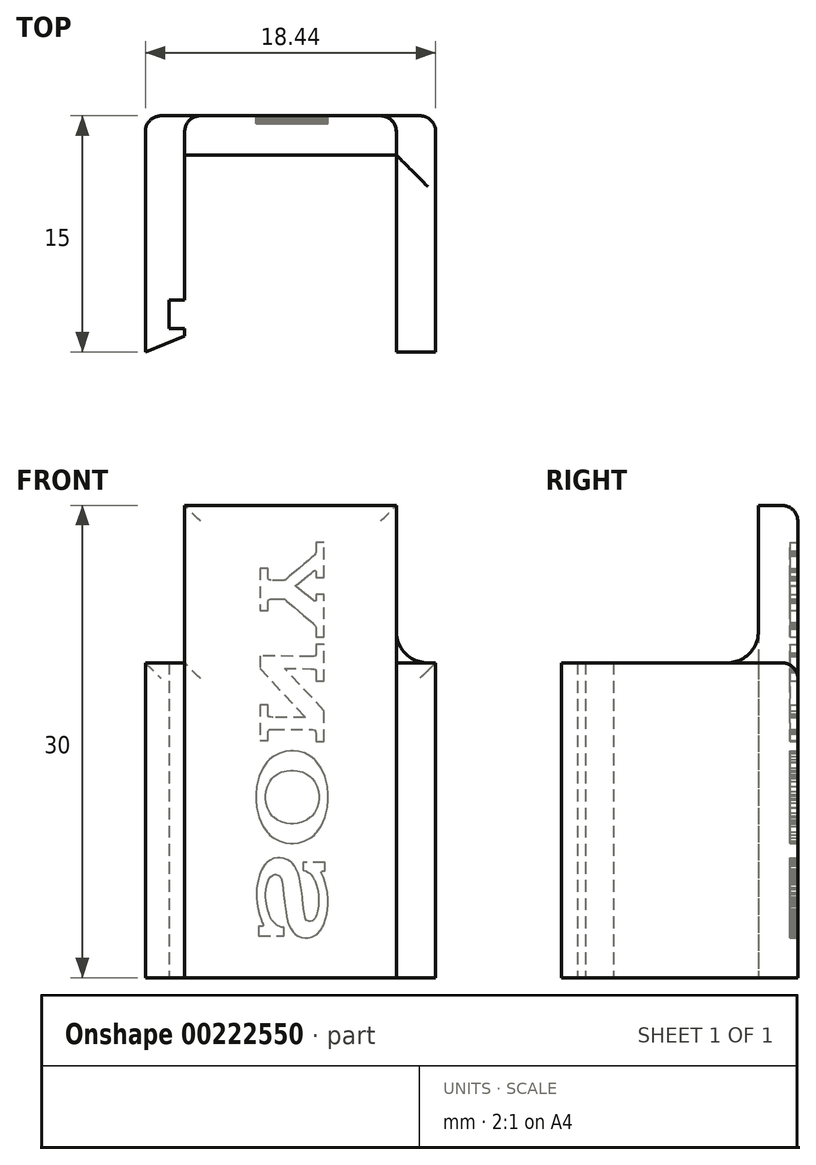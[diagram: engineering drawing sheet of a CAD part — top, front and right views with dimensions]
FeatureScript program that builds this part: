
annotation { "Feature Type Name" : "Feature", "Feature Type Description" : "" }
export const myFeature = defineFeature(function(context is Context, id is Id, definition is map)
    precondition{}
    {
        {
            var Q0;
            Q0=qCreatedBy(makeId("Top.planeOp"),FACE);
            var sketch = newSketch(context, id + "F0", { "sketchPlane" : qUnion([Q0])});
            skLineSegment(sketch, "E0", {"start": v(0, 0) * mm, "end": v(0, 1.5) * mm});
            skLineSegment(sketch, "E1", {"start": v(0, 12.5) * mm, "end": v(13.44, 12.5) * mm});
            skLineSegment(sketch, "E2", {"start": v(13.44, 0) * mm, "end": v(15.94, 0) * mm});
            skLineSegment(sketch, "E3", {"start": v(15.94, 0) * mm, "end": v(15.94, 15) * mm});
            skLineSegment(sketch, "E4", {"start": v(15.94, 15) * mm, "end": v(-2.5, 15) * mm});
            skLineSegment(sketch, "E5", {"start": v(-2.5, 15) * mm, "end": v(-2.5, 0) * mm});
            skLineSegment(sketch, "E6", {"start": v(-2.5, 0) * mm, "end": v(0, 0) * mm});
            skLineSegment(sketch, "E7", {"start": v(13.44, 12.5) * mm, "end": v(13.44, 0) * mm});
            skLineSegment(sketch, "E8", {"start": v(0, 1.5) * mm, "end": v(-1, 1.5) * mm});
            skLineSegment(sketch, "E9", {"start": v(-1, 1.5) * mm, "end": v(-1, 3.3) * mm});
            skLineSegment(sketch, "E10", {"start": v(-1, 3.3) * mm, "end": v(0, 3.3) * mm});
            skLineSegment(sketch, "E11.trimOffspring", {"start": v(0, 3.3) * mm, "end": v(0, 12.5) * mm});
            skSolve(sketch);
        }
        {
            var Q0;
            Q0 = qSketchRegion(id + "F0", true);
            extrude(context, id + "F1", {"entities" : qUnion([Q0]), "depth" : 20 * mm});
        }
        {
            var Q0;
            Q0=makeQuery(id+"F1.opExtrude","CAP_FACE",FACE,{"disambiguationData":[OSD([sQuery(id+"F0.wireOp",EDGE,"E0"),sQuery(id+"F0.wireOp",EDGE,"E1"),sQuery(id+"F0.wireOp",EDGE,"E2"),sQuery(id+"F0.wireOp",EDGE,"E3"),sQuery(id+"F0.wireOp",EDGE,"E4"),sQuery(id+"F0.wireOp",EDGE,"E5"),sQuery(id+"F0.wireOp",EDGE,"E6"),sQuery(id+"F0.wireOp",EDGE,"E7"),sQuery(id+"F0.wireOp",EDGE,"E8"),sQuery(id+"F0.wireOp",EDGE,"E9"),sQuery(id+"F0.wireOp",EDGE,"E10"),sQuery(id+"F0.wireOp",EDGE,"E11.trimOffspring")])],"isStart":false});
            var sketch = newSketch(context, id + "F2", { "sketchPlane" : qUnion([Q0])});
            skLineSegment(sketch, "E12.bottom", {"start": v(0, 15) * mm, "end": v(13.44, 15) * mm});
            skLineSegment(sketch, "E12.top", {"start": v(0, 12.5) * mm, "end": v(13.44, 12.5) * mm});
            skLineSegment(sketch, "E12.left", {"start": v(0, 15) * mm, "end": v(0, 12.5) * mm});
            skLineSegment(sketch, "E12.right", {"start": v(13.44, 15) * mm, "end": v(13.44, 12.5) * mm});
            skSolve(sketch);
        }
        {
            var Q0;
            Q0 = qSketchRegion(id + "F2", true);
            extrude(context, id + "F3", {"entities" : qUnion([Q0]), "operationType" : NewBodyOperationType.ADD, "depth" : 10 * mm});
        }
        {
            var Q0;
            Q0=makeQuery(id+"F3.boolean.opBoolean","MERGE",FACE,{"derivedFrom":[makeQuery(id+"F1.opExtrude","SWEPT_FACE",FACE,{"disambiguationData":[OSD([sQuery(id+"F0.wireOp",EDGE,"E4")])]}),makeQuery(id+"F3.opExtrude","SWEPT_FACE",FACE,{"disambiguationData":[OSD([sQuery(id+"F2.wireOp",EDGE,"E12.bottom")])]})]});
            var sketch = newSketch(context, id + "F4", { "sketchPlane" : qUnion([Q0])});
            skLineSegment(sketch, "E13", {"start": v(-8.35, 27.15) * mm, "end": v(-8.35, 27.12) * mm});
            skLineSegment(sketch, "E14", {"start": v(-8.35, 27.12) * mm, "end": v(-8.34, 27.03) * mm});
            skLineSegment(sketch, "E15", {"start": v(-8.34, 27.03) * mm, "end": v(-8.31, 26.94) * mm});
            skLineSegment(sketch, "E16", {"start": v(-8.31, 26.94) * mm, "end": v(-8.25, 26.85) * mm});
            skLineSegment(sketch, "E17", {"start": v(-8.25, 26.85) * mm, "end": v(-8.18, 26.78) * mm});
            skLineSegment(sketch, "E18", {"start": v(-8.18, 26.78) * mm, "end": v(-8.16, 26.76) * mm});
            skLineSegment(sketch, "E19", {"start": v(-8.16, 26.76) * mm, "end": v(-8.14, 26.75) * mm});
            skLineSegment(sketch, "E20", {"start": v(-8.14, 26.75) * mm, "end": v(-8.06, 26.68) * mm});
            skLineSegment(sketch, "E21", {"start": v(-8.06, 26.68) * mm, "end": v(-7.85, 26.5) * mm});
            skLineSegment(sketch, "E22", {"start": v(-7.85, 26.5) * mm, "end": v(-7.57, 26.27) * mm});
            skLineSegment(sketch, "E23", {"start": v(-7.57, 26.27) * mm, "end": v(-7.26, 26) * mm});
            skLineSegment(sketch, "E24", {"start": v(-7.26, 26) * mm, "end": v(-6.94, 25.74) * mm});
            skLineSegment(sketch, "E25", {"start": v(-6.94, 25.74) * mm, "end": v(-6.67, 25.5) * mm});
            skLineSegment(sketch, "E26", {"start": v(-6.67, 25.5) * mm, "end": v(-6.47, 25.34) * mm});
            skLineSegment(sketch, "E27", {"start": v(-6.47, 25.34) * mm, "end": v(-6.4, 25.28) * mm});
            skLineSegment(sketch, "E28", {"start": v(-6.4, 25.28) * mm, "end": v(-6.38, 25.27) * mm});
            skLineSegment(sketch, "E29", {"start": v(-6.38, 25.27) * mm, "end": v(-6.38, 25.26) * mm});
            skLineSegment(sketch, "E30", {"start": v(-6.38, 25.26) * mm, "end": v(-6.34, 25.25) * mm});
            skLineSegment(sketch, "E31", {"start": v(-6.34, 25.25) * mm, "end": v(-6.32, 25.25) * mm});
            skLineSegment(sketch, "E32", {"start": v(-6.32, 25.25) * mm, "end": v(-6.3, 25.25) * mm});
            skLineSegment(sketch, "E33", {"start": v(-6.3, 25.25) * mm, "end": v(-5.5, 25.25) * mm});
            skLineSegment(sketch, "E34", {"start": v(-5.5, 25.25) * mm, "end": v(-5.49, 25.25) * mm});
            skLineSegment(sketch, "E35", {"start": v(-5.49, 25.25) * mm, "end": v(-5.44, 25.25) * mm});
            skLineSegment(sketch, "E36", {"start": v(-5.44, 25.25) * mm, "end": v(-5.4, 25.26) * mm});
            skLineSegment(sketch, "E37", {"start": v(-5.4, 25.26) * mm, "end": v(-5.39, 25.26) * mm});
            skLineSegment(sketch, "E38", {"start": v(-5.39, 25.26) * mm, "end": v(-5.38, 25.26) * mm});
            skLineSegment(sketch, "E39", {"start": v(-5.38, 25.26) * mm, "end": v(-5.33, 25.3) * mm});
            skLineSegment(sketch, "E40", {"start": v(-5.33, 25.3) * mm, "end": v(-5.3, 25.35) * mm});
            skLineSegment(sketch, "E41", {"start": v(-5.3, 25.35) * mm, "end": v(-5.3, 25.37) * mm});
            skLineSegment(sketch, "E42", {"start": v(-5.3, 25.37) * mm, "end": v(-5.29, 25.37) * mm});
            skLineSegment(sketch, "E43", {"start": v(-5.29, 25.37) * mm, "end": v(-5.28, 25.43) * mm});
            skLineSegment(sketch, "E44", {"start": v(-5.28, 25.43) * mm, "end": v(-5.28, 25.48) * mm});
            skLineSegment(sketch, "E45", {"start": v(-5.28, 25.48) * mm, "end": v(-5.28, 25.5) * mm});
            skLineSegment(sketch, "E46", {"start": v(-5.28, 25.5) * mm, "end": v(-5.28, 26) * mm});
            skLineSegment(sketch, "E47", {"start": v(-5.28, 26) * mm, "end": v(-4.77, 26) * mm});
            skLineSegment(sketch, "E48", {"start": v(-4.77, 26) * mm, "end": v(-4.77, 23.31) * mm});
            skLineSegment(sketch, "E49", {"start": v(-4.77, 23.31) * mm, "end": v(-5.28, 23.31) * mm});
            skLineSegment(sketch, "E50", {"start": v(-5.28, 23.31) * mm, "end": v(-5.28, 23.8) * mm});
            skLineSegment(sketch, "E51", {"start": v(-5.28, 23.8) * mm, "end": v(-5.28, 23.81) * mm});
            skLineSegment(sketch, "E52", {"start": v(-5.28, 23.81) * mm, "end": v(-5.28, 23.86) * mm});
            skLineSegment(sketch, "E53", {"start": v(-5.28, 23.86) * mm, "end": v(-5.29, 23.93) * mm});
            skLineSegment(sketch, "E54", {"start": v(-5.29, 23.93) * mm, "end": v(-5.3, 23.93) * mm});
            skLineSegment(sketch, "E55", {"start": v(-5.3, 23.93) * mm, "end": v(-5.3, 23.94) * mm});
            skLineSegment(sketch, "E56", {"start": v(-5.3, 23.94) * mm, "end": v(-5.33, 24) * mm});
            skLineSegment(sketch, "E57", {"start": v(-5.33, 24) * mm, "end": v(-5.38, 24.03) * mm});
            skLineSegment(sketch, "E58", {"start": v(-5.38, 24.03) * mm, "end": v(-5.39, 24.04) * mm});
            skLineSegment(sketch, "E59", {"start": v(-5.39, 24.04) * mm, "end": v(-5.4, 24.04) * mm});
            skLineSegment(sketch, "E60", {"start": v(-5.4, 24.04) * mm, "end": v(-5.44, 24.05) * mm});
            skLineSegment(sketch, "E61", {"start": v(-5.44, 24.05) * mm, "end": v(-5.49, 24.05) * mm});
            skLineSegment(sketch, "E62", {"start": v(-5.49, 24.05) * mm, "end": v(-5.5, 24.05) * mm});
            skLineSegment(sketch, "E63", {"start": v(-5.5, 24.05) * mm, "end": v(-5.62, 24.05) * mm});
            skLineSegment(sketch, "E64", {"start": v(-5.62, 24.05) * mm, "end": v(-5.9, 24.05) * mm});
            skLineSegment(sketch, "E65", {"start": v(-5.9, 24.05) * mm, "end": v(-6.17, 24.05) * mm});
            skLineSegment(sketch, "E66", {"start": v(-6.17, 24.05) * mm, "end": v(-6.27, 24.05) * mm});
            skLineSegment(sketch, "E67", {"start": v(-6.27, 24.05) * mm, "end": v(-6.3, 24.05) * mm});
            skLineSegment(sketch, "E68", {"start": v(-6.3, 24.05) * mm, "end": v(-6.31, 24.05) * mm});
            skLineSegment(sketch, "E69", {"start": v(-6.31, 24.05) * mm, "end": v(-6.33, 24.04) * mm});
            skLineSegment(sketch, "E70", {"start": v(-6.33, 24.04) * mm, "end": v(-6.37, 24.02) * mm});
            skLineSegment(sketch, "E71", {"start": v(-6.37, 24.02) * mm, "end": v(-6.38, 24.02) * mm});
            skLineSegment(sketch, "E72", {"start": v(-6.38, 24.02) * mm, "end": v(-6.39, 24) * mm});
            skLineSegment(sketch, "E73", {"start": v(-6.39, 24) * mm, "end": v(-6.46, 23.94) * mm});
            skLineSegment(sketch, "E74", {"start": v(-6.46, 23.94) * mm, "end": v(-6.66, 23.78) * mm});
            skLineSegment(sketch, "E75", {"start": v(-6.66, 23.78) * mm, "end": v(-6.93, 23.55) * mm});
            skLineSegment(sketch, "E76", {"start": v(-6.93, 23.55) * mm, "end": v(-7.24, 23.29) * mm});
            skLineSegment(sketch, "E77", {"start": v(-7.24, 23.29) * mm, "end": v(-7.55, 23.02) * mm});
            skLineSegment(sketch, "E78", {"start": v(-7.55, 23.02) * mm, "end": v(-7.83, 22.79) * mm});
            skLineSegment(sketch, "E79", {"start": v(-7.83, 22.79) * mm, "end": v(-8.03, 22.62) * mm});
            skLineSegment(sketch, "E80", {"start": v(-8.03, 22.62) * mm, "end": v(-8.1, 22.55) * mm});
            skLineSegment(sketch, "E81", {"start": v(-8.1, 22.55) * mm, "end": v(-8.12, 22.54) * mm});
            skLineSegment(sketch, "E82", {"start": v(-8.12, 22.54) * mm, "end": v(-8.14, 22.52) * mm});
            skLineSegment(sketch, "E83", {"start": v(-8.14, 22.52) * mm, "end": v(-8.2, 22.47) * mm});
            skLineSegment(sketch, "E84", {"start": v(-8.2, 22.47) * mm, "end": v(-8.27, 22.37) * mm});
            skLineSegment(sketch, "E85", {"start": v(-8.27, 22.37) * mm, "end": v(-8.33, 22.26) * mm});
            skLineSegment(sketch, "E86", {"start": v(-8.33, 22.26) * mm, "end": v(-8.35, 22.15) * mm});
            skLineSegment(sketch, "E87", {"start": v(-8.35, 22.15) * mm, "end": v(-8.35, 22.11) * mm});
            skLineSegment(sketch, "E88", {"start": v(-8.35, 22.11) * mm, "end": v(-8.35, 21.63) * mm});
            skLineSegment(sketch, "E89", {"start": v(-8.35, 21.63) * mm, "end": v(-8.86, 21.63) * mm});
            skLineSegment(sketch, "E90", {"start": v(-8.86, 21.63) * mm, "end": v(-8.86, 24.34) * mm});
            skLineSegment(sketch, "E91", {"start": v(-8.86, 24.34) * mm, "end": v(-8.35, 24.34) * mm});
            skLineSegment(sketch, "E92", {"start": v(-8.35, 24.34) * mm, "end": v(-8.35, 24.01) * mm});
            skLineSegment(sketch, "E93", {"start": v(-8.35, 24.01) * mm, "end": v(-8.35, 24) * mm});
            skLineSegment(sketch, "E94", {"start": v(-8.35, 24) * mm, "end": v(-8.34, 23.96) * mm});
            skLineSegment(sketch, "E95", {"start": v(-8.34, 23.96) * mm, "end": v(-8.3, 23.93) * mm});
            skLineSegment(sketch, "E96", {"start": v(-8.3, 23.93) * mm, "end": v(-8.25, 23.92) * mm});
            skLineSegment(sketch, "E97", {"start": v(-8.25, 23.92) * mm, "end": v(-8.2, 23.94) * mm});
            skLineSegment(sketch, "E98", {"start": v(-8.2, 23.94) * mm, "end": v(-8.2, 23.95) * mm});
            skLineSegment(sketch, "E99", {"start": v(-8.2, 23.95) * mm, "end": v(-8.14, 24) * mm});
            skLineSegment(sketch, "E100", {"start": v(-8.14, 24) * mm, "end": v(-8.01, 24.1) * mm});
            skLineSegment(sketch, "E101", {"start": v(-8.01, 24.1) * mm, "end": v(-7.83, 24.24) * mm});
            skLineSegment(sketch, "E102", {"start": v(-7.83, 24.24) * mm, "end": v(-7.62, 24.4) * mm});
            skLineSegment(sketch, "E103", {"start": v(-7.62, 24.4) * mm, "end": v(-7.41, 24.58) * mm});
            skLineSegment(sketch, "E104", {"start": v(-7.41, 24.58) * mm, "end": v(-7.23, 24.73) * mm});
            skLineSegment(sketch, "E105", {"start": v(-7.23, 24.73) * mm, "end": v(-7.1, 24.83) * mm});
            skLineSegment(sketch, "E106", {"start": v(-7.1, 24.83) * mm, "end": v(-7.05, 24.87) * mm});
            skLineSegment(sketch, "E107", {"start": v(-7.05, 24.87) * mm, "end": v(-7.05, 24.87) * mm});
            skLineSegment(sketch, "E108", {"start": v(-7.05, 24.87) * mm, "end": v(-7.04, 24.87) * mm});
            skLineSegment(sketch, "E109", {"start": v(-7.04, 24.87) * mm, "end": v(-7.04, 24.9) * mm});
            skLineSegment(sketch, "E110", {"start": v(-7.04, 24.9) * mm, "end": v(-7.04, 24.9) * mm});
            skLineSegment(sketch, "E111", {"start": v(-7.04, 24.9) * mm, "end": v(-7.05, 24.9) * mm});
            skLineSegment(sketch, "E112", {"start": v(-7.05, 24.9) * mm, "end": v(-7.1, 24.94) * mm});
            skLineSegment(sketch, "E113", {"start": v(-7.1, 24.94) * mm, "end": v(-7.23, 25.05) * mm});
            skLineSegment(sketch, "E114", {"start": v(-7.23, 25.05) * mm, "end": v(-7.4, 25.2) * mm});
            skLineSegment(sketch, "E115", {"start": v(-7.4, 25.2) * mm, "end": v(-7.62, 25.37) * mm});
            skLineSegment(sketch, "E116", {"start": v(-7.62, 25.37) * mm, "end": v(-7.83, 25.54) * mm});
            skLineSegment(sketch, "E117", {"start": v(-7.83, 25.54) * mm, "end": v(-8, 25.7) * mm});
            skLineSegment(sketch, "E118", {"start": v(-8, 25.7) * mm, "end": v(-8.14, 25.8) * mm});
            skLineSegment(sketch, "E119", {"start": v(-8.14, 25.8) * mm, "end": v(-8.19, 25.84) * mm});
            skLineSegment(sketch, "E120", {"start": v(-8.19, 25.84) * mm, "end": v(-8.2, 25.84) * mm});
            skLineSegment(sketch, "E121", {"start": v(-8.2, 25.84) * mm, "end": v(-8.2, 25.85) * mm});
            skLineSegment(sketch, "E122", {"start": v(-8.2, 25.85) * mm, "end": v(-8.24, 25.86) * mm});
            skLineSegment(sketch, "E123", {"start": v(-8.24, 25.86) * mm, "end": v(-8.3, 25.85) * mm});
            skLineSegment(sketch, "E124", {"start": v(-8.3, 25.85) * mm, "end": v(-8.33, 25.82) * mm});
            skLineSegment(sketch, "E125", {"start": v(-8.33, 25.82) * mm, "end": v(-8.35, 25.78) * mm});
            skLineSegment(sketch, "E126", {"start": v(-8.35, 25.78) * mm, "end": v(-8.35, 25.76) * mm});
            skLineSegment(sketch, "E127", {"start": v(-8.35, 25.76) * mm, "end": v(-8.35, 25.43) * mm});
            skLineSegment(sketch, "E128", {"start": v(-8.35, 25.43) * mm, "end": v(-8.86, 25.43) * mm});
            skLineSegment(sketch, "E129", {"start": v(-8.86, 25.43) * mm, "end": v(-8.86, 27.65) * mm});
            skLineSegment(sketch, "E130", {"start": v(-8.86, 27.65) * mm, "end": v(-8.35, 27.65) * mm});
            skLineSegment(sketch, "E131", {"start": v(-8.35, 27.65) * mm, "end": v(-8.35, 27.15) * mm});
            skLineSegment(sketch, "E132", {"start": v(-8.03, 20.4) * mm, "end": v(-4.77, 20.45) * mm});
            skLineSegment(sketch, "E133", {"start": v(-4.77, 20.45) * mm, "end": v(-4.77, 19.66) * mm});
            skLineSegment(sketch, "E134", {"start": v(-4.77, 19.66) * mm, "end": v(-7.66, 16.54) * mm});
            skLineSegment(sketch, "E135", {"start": v(-7.66, 16.54) * mm, "end": v(-5.6, 16.55) * mm});
            skLineSegment(sketch, "E136", {"start": v(-5.6, 16.55) * mm, "end": v(-5.57, 16.55) * mm});
            skLineSegment(sketch, "E137", {"start": v(-5.57, 16.55) * mm, "end": v(-5.46, 16.55) * mm});
            skLineSegment(sketch, "E138", {"start": v(-5.46, 16.55) * mm, "end": v(-5.36, 16.58) * mm});
            skLineSegment(sketch, "E139", {"start": v(-5.36, 16.58) * mm, "end": v(-5.3, 16.65) * mm});
            skLineSegment(sketch, "E140", {"start": v(-5.3, 16.65) * mm, "end": v(-5.28, 16.75) * mm});
            skLineSegment(sketch, "E141", {"start": v(-5.28, 16.75) * mm, "end": v(-5.28, 16.78) * mm});
            skLineSegment(sketch, "E142", {"start": v(-5.28, 16.78) * mm, "end": v(-5.28, 17.33) * mm});
            skLineSegment(sketch, "E143", {"start": v(-5.28, 17.33) * mm, "end": v(-4.77, 17.33) * mm});
            skLineSegment(sketch, "E144", {"start": v(-4.77, 17.33) * mm, "end": v(-4.77, 15.07) * mm});
            skLineSegment(sketch, "E145", {"start": v(-4.77, 15.07) * mm, "end": v(-5.28, 15.07) * mm});
            skLineSegment(sketch, "E146", {"start": v(-5.28, 15.07) * mm, "end": v(-5.28, 15.6) * mm});
            skLineSegment(sketch, "E147", {"start": v(-5.28, 15.6) * mm, "end": v(-5.28, 15.62) * mm});
            skLineSegment(sketch, "E148", {"start": v(-5.28, 15.62) * mm, "end": v(-5.31, 15.7) * mm});
            skLineSegment(sketch, "E149", {"start": v(-5.31, 15.7) * mm, "end": v(-5.4, 15.76) * mm});
            skLineSegment(sketch, "E150", {"start": v(-5.4, 15.76) * mm, "end": v(-5.5, 15.78) * mm});
            skLineSegment(sketch, "E151", {"start": v(-5.5, 15.78) * mm, "end": v(-5.6, 15.79) * mm});
            skLineSegment(sketch, "E152", {"start": v(-5.6, 15.79) * mm, "end": v(-5.62, 15.79) * mm});
            skLineSegment(sketch, "E153", {"start": v(-5.62, 15.79) * mm, "end": v(-8.01, 15.79) * mm});
            skLineSegment(sketch, "E154", {"start": v(-8.01, 15.79) * mm, "end": v(-8.04, 15.79) * mm});
            skLineSegment(sketch, "E155", {"start": v(-8.04, 15.79) * mm, "end": v(-8.13, 15.78) * mm});
            skLineSegment(sketch, "E156", {"start": v(-8.13, 15.78) * mm, "end": v(-8.24, 15.74) * mm});
            skLineSegment(sketch, "E157", {"start": v(-8.24, 15.74) * mm, "end": v(-8.32, 15.64) * mm});
            skLineSegment(sketch, "E158", {"start": v(-8.32, 15.64) * mm, "end": v(-8.35, 15.5) * mm});
            skLineSegment(sketch, "E159", {"start": v(-8.35, 15.5) * mm, "end": v(-8.35, 15.45) * mm});
            skLineSegment(sketch, "E160", {"start": v(-8.35, 15.45) * mm, "end": v(-8.35, 15.02) * mm});
            skLineSegment(sketch, "E161", {"start": v(-8.35, 15.02) * mm, "end": v(-8.86, 15.02) * mm});
            skLineSegment(sketch, "E162", {"start": v(-8.86, 15.02) * mm, "end": v(-8.86, 16.96) * mm});
            skLineSegment(sketch, "E163", {"start": v(-8.86, 16.96) * mm, "end": v(-6.33, 19.66) * mm});
            skLineSegment(sketch, "E164", {"start": v(-6.33, 19.66) * mm, "end": v(-8.03, 19.63) * mm});
            skLineSegment(sketch, "E165", {"start": v(-8.03, 19.63) * mm, "end": v(-8.07, 19.63) * mm});
            skLineSegment(sketch, "E166", {"start": v(-8.07, 19.63) * mm, "end": v(-8.18, 19.62) * mm});
            skLineSegment(sketch, "E167", {"start": v(-8.18, 19.62) * mm, "end": v(-8.27, 19.58) * mm});
            skLineSegment(sketch, "E168", {"start": v(-8.27, 19.58) * mm, "end": v(-8.33, 19.5) * mm});
            skLineSegment(sketch, "E169", {"start": v(-8.33, 19.5) * mm, "end": v(-8.35, 19.39) * mm});
            skLineSegment(sketch, "E170", {"start": v(-8.35, 19.39) * mm, "end": v(-8.35, 19.35) * mm});
            skLineSegment(sketch, "E171", {"start": v(-8.35, 19.35) * mm, "end": v(-8.35, 18.85) * mm});
            skLineSegment(sketch, "E172", {"start": v(-8.35, 18.85) * mm, "end": v(-8.86, 18.85) * mm});
            skLineSegment(sketch, "E173", {"start": v(-8.86, 18.85) * mm, "end": v(-8.86, 21.16) * mm});
            skLineSegment(sketch, "E174", {"start": v(-8.86, 21.16) * mm, "end": v(-8.35, 21.16) * mm});
            skLineSegment(sketch, "E175", {"start": v(-8.35, 21.16) * mm, "end": v(-8.35, 20.66) * mm});
            skLineSegment(sketch, "E176", {"start": v(-8.35, 20.66) * mm, "end": v(-8.35, 20.62) * mm});
            skLineSegment(sketch, "E177", {"start": v(-8.35, 20.62) * mm, "end": v(-8.33, 20.52) * mm});
            skLineSegment(sketch, "E178", {"start": v(-8.33, 20.52) * mm, "end": v(-8.28, 20.44) * mm});
            skLineSegment(sketch, "E179", {"start": v(-8.28, 20.44) * mm, "end": v(-8.18, 20.41) * mm});
            skLineSegment(sketch, "E180", {"start": v(-8.18, 20.41) * mm, "end": v(-8.07, 20.4) * mm});
            skLineSegment(sketch, "E181", {"start": v(-8.07, 20.4) * mm, "end": v(-8.03, 20.4) * mm});
            skLineSegment(sketch, "E182", {"start": v(-4.52, 11.47) * mm, "end": v(-4.52, 11.3) * mm});
            skLineSegment(sketch, "E183", {"start": v(-4.52, 11.3) * mm, "end": v(-4.57, 10.8) * mm});
            skLineSegment(sketch, "E184", {"start": v(-4.57, 10.8) * mm, "end": v(-4.72, 10.18) * mm});
            skLineSegment(sketch, "E185", {"start": v(-4.72, 10.18) * mm, "end": v(-4.98, 9.63) * mm});
            skLineSegment(sketch, "E186", {"start": v(-4.98, 9.63) * mm, "end": v(-5.23, 9.26) * mm});
            skLineSegment(sketch, "E187", {"start": v(-5.23, 9.26) * mm, "end": v(-5.33, 9.15) * mm});
            skLineSegment(sketch, "E188", {"start": v(-5.33, 9.15) * mm, "end": v(-5.4, 9.08) * mm});
            skLineSegment(sketch, "E189", {"start": v(-5.4, 9.08) * mm, "end": v(-5.65, 8.88) * mm});
            skLineSegment(sketch, "E190", {"start": v(-5.65, 8.88) * mm, "end": v(-6.01, 8.68) * mm});
            skLineSegment(sketch, "E191", {"start": v(-6.01, 8.68) * mm, "end": v(-6.4, 8.56) * mm});
            skLineSegment(sketch, "E192", {"start": v(-6.4, 8.56) * mm, "end": v(-6.72, 8.52) * mm});
            skLineSegment(sketch, "E193", {"start": v(-6.72, 8.52) * mm, "end": v(-6.82, 8.52) * mm});
            skLineSegment(sketch, "E194", {"start": v(-6.82, 8.52) * mm, "end": v(-6.92, 8.52) * mm});
            skLineSegment(sketch, "E195", {"start": v(-6.92, 8.52) * mm, "end": v(-7.23, 8.56) * mm});
            skLineSegment(sketch, "E196", {"start": v(-7.23, 8.56) * mm, "end": v(-7.62, 8.68) * mm});
            skLineSegment(sketch, "E197", {"start": v(-7.62, 8.68) * mm, "end": v(-7.99, 8.88) * mm});
            skLineSegment(sketch, "E198", {"start": v(-7.99, 8.88) * mm, "end": v(-8.24, 9.08) * mm});
            skLineSegment(sketch, "E199", {"start": v(-8.24, 9.08) * mm, "end": v(-8.3, 9.15) * mm});
            skLineSegment(sketch, "E200", {"start": v(-8.3, 9.15) * mm, "end": v(-8.4, 9.26) * mm});
            skLineSegment(sketch, "E201", {"start": v(-8.4, 9.26) * mm, "end": v(-8.65, 9.62) * mm});
            skLineSegment(sketch, "E202", {"start": v(-8.65, 9.62) * mm, "end": v(-8.9, 10.18) * mm});
            skLineSegment(sketch, "E203", {"start": v(-8.9, 10.18) * mm, "end": v(-9.06, 10.82) * mm});
            skLineSegment(sketch, "E204", {"start": v(-9.06, 10.82) * mm, "end": v(-9.12, 11.3) * mm});
            skLineSegment(sketch, "E205", {"start": v(-9.12, 11.3) * mm, "end": v(-9.12, 11.47) * mm});
            skLineSegment(sketch, "E206", {"start": v(-9.12, 11.47) * mm, "end": v(-9.12, 11.64) * mm});
            skLineSegment(sketch, "E207", {"start": v(-9.12, 11.64) * mm, "end": v(-9.07, 12.16) * mm});
            skLineSegment(sketch, "E208", {"start": v(-9.07, 12.16) * mm, "end": v(-8.92, 12.78) * mm});
            skLineSegment(sketch, "E209", {"start": v(-8.92, 12.78) * mm, "end": v(-8.67, 13.32) * mm});
            skLineSegment(sketch, "E210", {"start": v(-8.67, 13.32) * mm, "end": v(-8.41, 13.69) * mm});
            skLineSegment(sketch, "E211", {"start": v(-8.41, 13.69) * mm, "end": v(-8.3, 13.8) * mm});
            skLineSegment(sketch, "E212", {"start": v(-8.3, 13.8) * mm, "end": v(-8.24, 13.87) * mm});
            skLineSegment(sketch, "E213", {"start": v(-8.24, 13.87) * mm, "end": v(-7.99, 14.07) * mm});
            skLineSegment(sketch, "E214", {"start": v(-7.99, 14.07) * mm, "end": v(-7.62, 14.26) * mm});
            skLineSegment(sketch, "E215", {"start": v(-7.62, 14.26) * mm, "end": v(-7.23, 14.38) * mm});
            skLineSegment(sketch, "E216", {"start": v(-7.23, 14.38) * mm, "end": v(-6.92, 14.42) * mm});
            skLineSegment(sketch, "E217", {"start": v(-6.92, 14.42) * mm, "end": v(-6.82, 14.42) * mm});
            skLineSegment(sketch, "E218", {"start": v(-6.82, 14.42) * mm, "end": v(-6.72, 14.42) * mm});
            skLineSegment(sketch, "E219", {"start": v(-6.72, 14.42) * mm, "end": v(-6.42, 14.38) * mm});
            skLineSegment(sketch, "E220", {"start": v(-6.42, 14.38) * mm, "end": v(-6.02, 14.26) * mm});
            skLineSegment(sketch, "E221", {"start": v(-6.02, 14.26) * mm, "end": v(-5.65, 14.07) * mm});
            skLineSegment(sketch, "E222", {"start": v(-5.65, 14.07) * mm, "end": v(-5.4, 13.87) * mm});
            skLineSegment(sketch, "E223", {"start": v(-5.4, 13.87) * mm, "end": v(-5.33, 13.8) * mm});
            skLineSegment(sketch, "E224", {"start": v(-5.33, 13.8) * mm, "end": v(-5.23, 13.7) * mm});
            skLineSegment(sketch, "E225", {"start": v(-5.23, 13.7) * mm, "end": v(-4.98, 13.33) * mm});
            skLineSegment(sketch, "E226", {"start": v(-4.98, 13.33) * mm, "end": v(-4.72, 12.77) * mm});
            skLineSegment(sketch, "E227", {"start": v(-4.72, 12.77) * mm, "end": v(-4.57, 12.14) * mm});
            skLineSegment(sketch, "E228", {"start": v(-4.57, 12.14) * mm, "end": v(-4.52, 11.64) * mm});
            skLineSegment(sketch, "E229", {"start": v(-4.52, 11.64) * mm, "end": v(-4.52, 11.47) * mm});
            skLineSegment(sketch, "E230", {"start": v(-8.02, 12.72) * mm, "end": v(-8.08, 12.66) * mm});
            skLineSegment(sketch, "E231", {"start": v(-8.08, 12.66) * mm, "end": v(-8.23, 12.46) * mm});
            skLineSegment(sketch, "E232", {"start": v(-8.23, 12.46) * mm, "end": v(-8.39, 12.16) * mm});
            skLineSegment(sketch, "E233", {"start": v(-8.39, 12.16) * mm, "end": v(-8.49, 11.82) * mm});
            skLineSegment(sketch, "E234", {"start": v(-8.49, 11.82) * mm, "end": v(-8.52, 11.56) * mm});
            skLineSegment(sketch, "E235", {"start": v(-8.52, 11.56) * mm, "end": v(-8.52, 11.47) * mm});
            skLineSegment(sketch, "E236", {"start": v(-8.52, 11.47) * mm, "end": v(-8.52, 11.38) * mm});
            skLineSegment(sketch, "E237", {"start": v(-8.52, 11.38) * mm, "end": v(-8.49, 11.12) * mm});
            skLineSegment(sketch, "E238", {"start": v(-8.49, 11.12) * mm, "end": v(-8.4, 10.79) * mm});
            skLineSegment(sketch, "E239", {"start": v(-8.4, 10.79) * mm, "end": v(-8.24, 10.48) * mm});
            skLineSegment(sketch, "E240", {"start": v(-8.24, 10.48) * mm, "end": v(-8.08, 10.28) * mm});
            skLineSegment(sketch, "E241", {"start": v(-8.08, 10.28) * mm, "end": v(-8.02, 10.23) * mm});
            skLineSegment(sketch, "E242", {"start": v(-8.02, 10.23) * mm, "end": v(-7.97, 10.17) * mm});
            skLineSegment(sketch, "E243", {"start": v(-7.97, 10.17) * mm, "end": v(-7.77, 10.03) * mm});
            skLineSegment(sketch, "E244", {"start": v(-7.77, 10.03) * mm, "end": v(-7.48, 9.89) * mm});
            skLineSegment(sketch, "E245", {"start": v(-7.48, 9.89) * mm, "end": v(-7.16, 9.8) * mm});
            skLineSegment(sketch, "E246", {"start": v(-7.16, 9.8) * mm, "end": v(-6.9, 9.77) * mm});
            skLineSegment(sketch, "E247", {"start": v(-6.9, 9.77) * mm, "end": v(-6.82, 9.77) * mm});
            skLineSegment(sketch, "E248", {"start": v(-6.82, 9.77) * mm, "end": v(-6.74, 9.77) * mm});
            skLineSegment(sketch, "E249", {"start": v(-6.74, 9.77) * mm, "end": v(-6.48, 9.8) * mm});
            skLineSegment(sketch, "E250", {"start": v(-6.48, 9.8) * mm, "end": v(-6.16, 9.89) * mm});
            skLineSegment(sketch, "E251", {"start": v(-6.16, 9.89) * mm, "end": v(-5.87, 10.03) * mm});
            skLineSegment(sketch, "E252", {"start": v(-5.87, 10.03) * mm, "end": v(-5.68, 10.17) * mm});
            skLineSegment(sketch, "E253", {"start": v(-5.68, 10.17) * mm, "end": v(-5.62, 10.23) * mm});
            skLineSegment(sketch, "E254", {"start": v(-5.62, 10.23) * mm, "end": v(-5.56, 10.28) * mm});
            skLineSegment(sketch, "E255", {"start": v(-5.56, 10.28) * mm, "end": v(-5.4, 10.48) * mm});
            skLineSegment(sketch, "E256", {"start": v(-5.4, 10.48) * mm, "end": v(-5.25, 10.79) * mm});
            skLineSegment(sketch, "E257", {"start": v(-5.25, 10.79) * mm, "end": v(-5.16, 11.12) * mm});
            skLineSegment(sketch, "E258", {"start": v(-5.16, 11.12) * mm, "end": v(-5.12, 11.38) * mm});
            skLineSegment(sketch, "E259", {"start": v(-5.12, 11.38) * mm, "end": v(-5.12, 11.47) * mm});
            skLineSegment(sketch, "E260", {"start": v(-5.12, 11.47) * mm, "end": v(-5.12, 11.56) * mm});
            skLineSegment(sketch, "E261", {"start": v(-5.12, 11.56) * mm, "end": v(-5.16, 11.83) * mm});
            skLineSegment(sketch, "E262", {"start": v(-5.16, 11.83) * mm, "end": v(-5.25, 12.16) * mm});
            skLineSegment(sketch, "E263", {"start": v(-5.25, 12.16) * mm, "end": v(-5.4, 12.46) * mm});
            skLineSegment(sketch, "E264", {"start": v(-5.4, 12.46) * mm, "end": v(-5.56, 12.66) * mm});
            skLineSegment(sketch, "E265", {"start": v(-5.56, 12.66) * mm, "end": v(-5.62, 12.72) * mm});
            skLineSegment(sketch, "E266", {"start": v(-5.62, 12.72) * mm, "end": v(-5.68, 12.77) * mm});
            skLineSegment(sketch, "E267", {"start": v(-5.68, 12.77) * mm, "end": v(-5.88, 12.92) * mm});
            skLineSegment(sketch, "E268", {"start": v(-5.88, 12.92) * mm, "end": v(-6.16, 13.06) * mm});
            skLineSegment(sketch, "E269", {"start": v(-6.16, 13.06) * mm, "end": v(-6.47, 13.15) * mm});
            skLineSegment(sketch, "E270", {"start": v(-6.47, 13.15) * mm, "end": v(-6.73, 13.17) * mm});
            skLineSegment(sketch, "E271", {"start": v(-6.73, 13.17) * mm, "end": v(-6.82, 13.17) * mm});
            skLineSegment(sketch, "E272", {"start": v(-6.82, 13.17) * mm, "end": v(-6.9, 13.17) * mm});
            skLineSegment(sketch, "E273", {"start": v(-6.9, 13.17) * mm, "end": v(-7.16, 13.14) * mm});
            skLineSegment(sketch, "E274", {"start": v(-7.16, 13.14) * mm, "end": v(-7.48, 13.06) * mm});
            skLineSegment(sketch, "E275", {"start": v(-7.48, 13.06) * mm, "end": v(-7.77, 12.91) * mm});
            skLineSegment(sketch, "E276", {"start": v(-7.77, 12.91) * mm, "end": v(-7.97, 12.77) * mm});
            skLineSegment(sketch, "E277", {"start": v(-7.97, 12.77) * mm, "end": v(-8.02, 12.72) * mm});
            skLineSegment(sketch, "E278", {"start": v(-7.48, 5.03) * mm, "end": v(-7.47, 5.1) * mm});
            skLineSegment(sketch, "E279", {"start": v(-7.47, 5.1) * mm, "end": v(-7.44, 5.34) * mm});
            skLineSegment(sketch, "E280", {"start": v(-7.44, 5.34) * mm, "end": v(-7.39, 5.73) * mm});
            skLineSegment(sketch, "E281", {"start": v(-7.39, 5.73) * mm, "end": v(-7.33, 6.1) * mm});
            skLineSegment(sketch, "E282", {"start": v(-7.33, 6.1) * mm, "end": v(-7.28, 6.33) * mm});
            skLineSegment(sketch, "E283", {"start": v(-7.28, 6.33) * mm, "end": v(-7.26, 6.4) * mm});
            skLineSegment(sketch, "E284", {"start": v(-7.26, 6.4) * mm, "end": v(-7.25, 6.44) * mm});
            skLineSegment(sketch, "E285", {"start": v(-7.25, 6.44) * mm, "end": v(-7.18, 6.66) * mm});
            skLineSegment(sketch, "E286", {"start": v(-7.18, 6.66) * mm, "end": v(-7.1, 6.86) * mm});
            skLineSegment(sketch, "E287", {"start": v(-7.1, 6.86) * mm, "end": v(-7.08, 6.9) * mm});
            skLineSegment(sketch, "E288", {"start": v(-7.08, 6.9) * mm, "end": v(-7.07, 6.93) * mm});
            skLineSegment(sketch, "E289", {"start": v(-7.07, 6.93) * mm, "end": v(-6.96, 7.1) * mm});
            skLineSegment(sketch, "E290", {"start": v(-6.96, 7.1) * mm, "end": v(-6.83, 7.26) * mm});
            skLineSegment(sketch, "E291", {"start": v(-6.83, 7.26) * mm, "end": v(-6.8, 7.3) * mm});
            skLineSegment(sketch, "E292", {"start": v(-6.8, 7.3) * mm, "end": v(-6.78, 7.31) * mm});
            skLineSegment(sketch, "E293", {"start": v(-6.78, 7.31) * mm, "end": v(-6.7, 7.38) * mm});
            skLineSegment(sketch, "E294", {"start": v(-6.7, 7.38) * mm, "end": v(-6.53, 7.48) * mm});
            skLineSegment(sketch, "E295", {"start": v(-6.53, 7.48) * mm, "end": v(-6.28, 7.57) * mm});
            skLineSegment(sketch, "E296", {"start": v(-6.28, 7.57) * mm, "end": v(-6.05, 7.61) * mm});
            skLineSegment(sketch, "E297", {"start": v(-6.05, 7.61) * mm, "end": v(-5.97, 7.61) * mm});
            skLineSegment(sketch, "E298", {"start": v(-5.97, 7.61) * mm, "end": v(-5.9, 7.61) * mm});
            skLineSegment(sketch, "E299", {"start": v(-5.9, 7.61) * mm, "end": v(-5.65, 7.57) * mm});
            skLineSegment(sketch, "E300", {"start": v(-5.65, 7.57) * mm, "end": v(-5.4, 7.46) * mm});
            skLineSegment(sketch, "E301", {"start": v(-5.4, 7.46) * mm, "end": v(-5.23, 7.33) * mm});
            skLineSegment(sketch, "E302", {"start": v(-5.23, 7.33) * mm, "end": v(-5.15, 7.24) * mm});
            skLineSegment(sketch, "E303", {"start": v(-5.15, 7.24) * mm, "end": v(-5.12, 7.21) * mm});
            skLineSegment(sketch, "E304", {"start": v(-5.12, 7.21) * mm, "end": v(-5.08, 7.16) * mm});
            skLineSegment(sketch, "E305", {"start": v(-5.08, 7.16) * mm, "end": v(-4.89, 6.84) * mm});
            skLineSegment(sketch, "E306", {"start": v(-4.89, 6.84) * mm, "end": v(-4.76, 6.53) * mm});
            skLineSegment(sketch, "E307", {"start": v(-4.76, 6.53) * mm, "end": v(-4.74, 6.47) * mm});
            skLineSegment(sketch, "E308", {"start": v(-4.74, 6.47) * mm, "end": v(-4.73, 6.42) * mm});
            skLineSegment(sketch, "E309", {"start": v(-4.73, 6.42) * mm, "end": v(-4.68, 6.27) * mm});
            skLineSegment(sketch, "E310", {"start": v(-4.68, 6.27) * mm, "end": v(-4.62, 6) * mm});
            skLineSegment(sketch, "E311", {"start": v(-4.62, 6) * mm, "end": v(-4.58, 5.66) * mm});
            skLineSegment(sketch, "E312", {"start": v(-4.58, 5.66) * mm, "end": v(-4.56, 5.33) * mm});
            skLineSegment(sketch, "E313", {"start": v(-4.56, 5.33) * mm, "end": v(-4.56, 5.22) * mm});
            skLineSegment(sketch, "E314", {"start": v(-4.56, 5.22) * mm, "end": v(-4.56, 5.1) * mm});
            skLineSegment(sketch, "E315", {"start": v(-4.56, 5.1) * mm, "end": v(-4.6, 4.73) * mm});
            skLineSegment(sketch, "E316", {"start": v(-4.6, 4.73) * mm, "end": v(-4.66, 4.37) * mm});
            skLineSegment(sketch, "E317", {"start": v(-4.66, 4.37) * mm, "end": v(-4.68, 4.3) * mm});
            skLineSegment(sketch, "E318", {"start": v(-4.68, 4.3) * mm, "end": v(-4.7, 4.22) * mm});
            skLineSegment(sketch, "E319", {"start": v(-4.7, 4.22) * mm, "end": v(-4.75, 4) * mm});
            skLineSegment(sketch, "E320", {"start": v(-4.75, 4) * mm, "end": v(-4.84, 3.74) * mm});
            skLineSegment(sketch, "E321", {"start": v(-4.84, 3.74) * mm, "end": v(-4.92, 3.53) * mm});
            skLineSegment(sketch, "E322", {"start": v(-4.92, 3.53) * mm, "end": v(-4.97, 3.42) * mm});
            skLineSegment(sketch, "E323", {"start": v(-4.97, 3.42) * mm, "end": v(-4.98, 3.4) * mm});
            skLineSegment(sketch, "E324", {"start": v(-4.98, 3.4) * mm, "end": v(-4.99, 3.38) * mm});
            skLineSegment(sketch, "E325", {"start": v(-4.99, 3.38) * mm, "end": v(-5, 3.33) * mm});
            skLineSegment(sketch, "E326", {"start": v(-5, 3.33) * mm, "end": v(-4.97, 3.29) * mm});
            skLineSegment(sketch, "E327", {"start": v(-4.97, 3.29) * mm, "end": v(-4.93, 3.27) * mm});
            skLineSegment(sketch, "E328", {"start": v(-4.93, 3.27) * mm, "end": v(-4.91, 3.26) * mm});
            skLineSegment(sketch, "E329", {"start": v(-4.91, 3.26) * mm, "end": v(-4.9, 3.26) * mm});
            skLineSegment(sketch, "E330", {"start": v(-4.9, 3.26) * mm, "end": v(-4.69, 3.26) * mm});
            skLineSegment(sketch, "E331", {"start": v(-4.69, 3.26) * mm, "end": v(-4.69, 2.65) * mm});
            skLineSegment(sketch, "E332", {"start": v(-4.69, 2.65) * mm, "end": v(-6.3, 2.65) * mm});
            skLineSegment(sketch, "E333", {"start": v(-6.3, 2.65) * mm, "end": v(-6.3, 3.2) * mm});
            skLineSegment(sketch, "E334", {"start": v(-6.3, 3.2) * mm, "end": v(-6.26, 3.2) * mm});
            skLineSegment(sketch, "E335", {"start": v(-6.26, 3.2) * mm, "end": v(-6.15, 3.21) * mm});
            skLineSegment(sketch, "E336", {"start": v(-6.15, 3.21) * mm, "end": v(-6.02, 3.25) * mm});
            skLineSegment(sketch, "E337", {"start": v(-6.02, 3.25) * mm, "end": v(-5.92, 3.3) * mm});
            skLineSegment(sketch, "E338", {"start": v(-5.92, 3.3) * mm, "end": v(-5.86, 3.33) * mm});
            skLineSegment(sketch, "E339", {"start": v(-5.86, 3.33) * mm, "end": v(-5.84, 3.34) * mm});
            skLineSegment(sketch, "E340", {"start": v(-5.84, 3.34) * mm, "end": v(-5.8, 3.38) * mm});
            skLineSegment(sketch, "E341", {"start": v(-5.8, 3.38) * mm, "end": v(-5.66, 3.51) * mm});
            skLineSegment(sketch, "E342", {"start": v(-5.66, 3.51) * mm, "end": v(-5.53, 3.68) * mm});
            skLineSegment(sketch, "E343", {"start": v(-5.53, 3.68) * mm, "end": v(-5.43, 3.86) * mm});
            skLineSegment(sketch, "E344", {"start": v(-5.43, 3.86) * mm, "end": v(-5.38, 3.99) * mm});
            skLineSegment(sketch, "E345", {"start": v(-5.38, 3.99) * mm, "end": v(-5.36, 4.03) * mm});
            skLineSegment(sketch, "E346", {"start": v(-5.36, 4.03) * mm, "end": v(-5.34, 4.08) * mm});
            skLineSegment(sketch, "E347", {"start": v(-5.34, 4.08) * mm, "end": v(-5.3, 4.24) * mm});
            skLineSegment(sketch, "E348", {"start": v(-5.3, 4.24) * mm, "end": v(-5.23, 4.53) * mm});
            skLineSegment(sketch, "E349", {"start": v(-5.23, 4.53) * mm, "end": v(-5.17, 4.87) * mm});
            skLineSegment(sketch, "E350", {"start": v(-5.17, 4.87) * mm, "end": v(-5.15, 5.13) * mm});
            skLineSegment(sketch, "E351", {"start": v(-5.15, 5.13) * mm, "end": v(-5.15, 5.22) * mm});
            skLineSegment(sketch, "E352", {"start": v(-5.15, 5.22) * mm, "end": v(-5.15, 5.32) * mm});
            skLineSegment(sketch, "E353", {"start": v(-5.15, 5.32) * mm, "end": v(-5.17, 5.63) * mm});
            skLineSegment(sketch, "E354", {"start": v(-5.17, 5.63) * mm, "end": v(-5.23, 5.93) * mm});
            skLineSegment(sketch, "E355", {"start": v(-5.23, 5.93) * mm, "end": v(-5.3, 6.13) * mm});
            skLineSegment(sketch, "E356", {"start": v(-5.3, 6.13) * mm, "end": v(-5.33, 6.2) * mm});
            skLineSegment(sketch, "E357", {"start": v(-5.33, 6.2) * mm, "end": v(-5.33, 6.22) * mm});
            skLineSegment(sketch, "E358", {"start": v(-5.33, 6.22) * mm, "end": v(-5.34, 6.23) * mm});
            skLineSegment(sketch, "E359", {"start": v(-5.34, 6.23) * mm, "end": v(-5.36, 6.3) * mm});
            skLineSegment(sketch, "E360", {"start": v(-5.36, 6.3) * mm, "end": v(-5.44, 6.4) * mm});
            skLineSegment(sketch, "E361", {"start": v(-5.44, 6.4) * mm, "end": v(-5.56, 6.5) * mm});
            skLineSegment(sketch, "E362", {"start": v(-5.56, 6.5) * mm, "end": v(-5.71, 6.55) * mm});
            skLineSegment(sketch, "E363", {"start": v(-5.71, 6.55) * mm, "end": v(-5.76, 6.55) * mm});
            skLineSegment(sketch, "E364", {"start": v(-5.76, 6.55) * mm, "end": v(-5.79, 6.55) * mm});
            skLineSegment(sketch, "E365", {"start": v(-5.79, 6.55) * mm, "end": v(-5.87, 6.54) * mm});
            skLineSegment(sketch, "E366", {"start": v(-5.87, 6.54) * mm, "end": v(-5.95, 6.5) * mm});
            skLineSegment(sketch, "E367", {"start": v(-5.95, 6.5) * mm, "end": v(-6.02, 6.46) * mm});
            skLineSegment(sketch, "E368", {"start": v(-6.02, 6.46) * mm, "end": v(-6.07, 6.4) * mm});
            skLineSegment(sketch, "E369", {"start": v(-6.07, 6.4) * mm, "end": v(-6.1, 6.33) * mm});
            skLineSegment(sketch, "E370", {"start": v(-6.1, 6.33) * mm, "end": v(-6.13, 6.26) * mm});
            skLineSegment(sketch, "E371", {"start": v(-6.13, 6.26) * mm, "end": v(-6.16, 6.19) * mm});
            skLineSegment(sketch, "E372", {"start": v(-6.16, 6.19) * mm, "end": v(-6.17, 6.14) * mm});
            skLineSegment(sketch, "E373", {"start": v(-6.17, 6.14) * mm, "end": v(-6.17, 6.12) * mm});
            skLineSegment(sketch, "E374", {"start": v(-6.17, 6.12) * mm, "end": v(-6.19, 6.07) * mm});
            skLineSegment(sketch, "E375", {"start": v(-6.19, 6.07) * mm, "end": v(-6.21, 5.92) * mm});
            skLineSegment(sketch, "E376", {"start": v(-6.21, 5.92) * mm, "end": v(-6.25, 5.64) * mm});
            skLineSegment(sketch, "E377", {"start": v(-6.25, 5.64) * mm, "end": v(-6.3, 5.3) * mm});
            skLineSegment(sketch, "E378", {"start": v(-6.3, 5.3) * mm, "end": v(-6.32, 5.02) * mm});
            skLineSegment(sketch, "E379", {"start": v(-6.32, 5.02) * mm, "end": v(-6.33, 4.92) * mm});
            skLineSegment(sketch, "E380", {"start": v(-6.33, 4.92) * mm, "end": v(-6.34, 4.83) * mm});
            skLineSegment(sketch, "E381", {"start": v(-6.34, 4.83) * mm, "end": v(-6.38, 4.55) * mm});
            skLineSegment(sketch, "E382", {"start": v(-6.38, 4.55) * mm, "end": v(-6.43, 4.2) * mm});
            skLineSegment(sketch, "E383", {"start": v(-6.43, 4.2) * mm, "end": v(-6.48, 3.9) * mm});
            skLineSegment(sketch, "E384", {"start": v(-6.48, 3.9) * mm, "end": v(-6.51, 3.73) * mm});
            skLineSegment(sketch, "E385", {"start": v(-6.51, 3.73) * mm, "end": v(-6.52, 3.67) * mm});
            skLineSegment(sketch, "E386", {"start": v(-6.52, 3.67) * mm, "end": v(-6.54, 3.59) * mm});
            skLineSegment(sketch, "E387", {"start": v(-6.54, 3.59) * mm, "end": v(-6.63, 3.33) * mm});
            skLineSegment(sketch, "E388", {"start": v(-6.63, 3.33) * mm, "end": v(-6.75, 3.1) * mm});
            skLineSegment(sketch, "E389", {"start": v(-6.75, 3.1) * mm, "end": v(-6.87, 2.92) * mm});
            skLineSegment(sketch, "E390", {"start": v(-6.87, 2.92) * mm, "end": v(-6.95, 2.84) * mm});
            skLineSegment(sketch, "E391", {"start": v(-6.95, 2.84) * mm, "end": v(-6.97, 2.81) * mm});
            skLineSegment(sketch, "E392", {"start": v(-6.97, 2.81) * mm, "end": v(-7.02, 2.77) * mm});
            skLineSegment(sketch, "E393", {"start": v(-7.02, 2.77) * mm, "end": v(-7.17, 2.67) * mm});
            skLineSegment(sketch, "E394", {"start": v(-7.17, 2.67) * mm, "end": v(-7.41, 2.57) * mm});
            skLineSegment(sketch, "E395", {"start": v(-7.41, 2.57) * mm, "end": v(-7.65, 2.52) * mm});
            skLineSegment(sketch, "E396", {"start": v(-7.65, 2.52) * mm, "end": v(-7.74, 2.52) * mm});
            skLineSegment(sketch, "E397", {"start": v(-7.74, 2.52) * mm, "end": v(-7.83, 2.52) * mm});
            skLineSegment(sketch, "E398", {"start": v(-7.83, 2.52) * mm, "end": v(-8.1, 2.59) * mm});
            skLineSegment(sketch, "E399", {"start": v(-8.1, 2.59) * mm, "end": v(-8.4, 2.75) * mm});
            skLineSegment(sketch, "E400", {"start": v(-8.4, 2.75) * mm, "end": v(-8.63, 3) * mm});
            skLineSegment(sketch, "E401", {"start": v(-8.63, 3) * mm, "end": v(-8.76, 3.23) * mm});
            skLineSegment(sketch, "E402", {"start": v(-8.76, 3.23) * mm, "end": v(-8.8, 3.31) * mm});
            skLineSegment(sketch, "E403", {"start": v(-8.8, 3.31) * mm, "end": v(-8.86, 3.43) * mm});
            skLineSegment(sketch, "E404", {"start": v(-8.86, 3.43) * mm, "end": v(-9.04, 4.06) * mm});
            skLineSegment(sketch, "E405", {"start": v(-9.04, 4.06) * mm, "end": v(-9.11, 4.63) * mm});
            skLineSegment(sketch, "E406", {"start": v(-9.11, 4.63) * mm, "end": v(-9.11, 4.82) * mm});
            skLineSegment(sketch, "E407", {"start": v(-9.11, 4.82) * mm, "end": v(-9.11, 4.97) * mm});
            skLineSegment(sketch, "E408", {"start": v(-9.11, 4.97) * mm, "end": v(-9.07, 5.43) * mm});
            skLineSegment(sketch, "E409", {"start": v(-9.07, 5.43) * mm, "end": v(-8.95, 5.95) * mm});
            skLineSegment(sketch, "E410", {"start": v(-8.95, 5.95) * mm, "end": v(-8.81, 6.36) * mm});
            skLineSegment(sketch, "E411", {"start": v(-8.81, 6.36) * mm, "end": v(-8.72, 6.57) * mm});
            skLineSegment(sketch, "E412", {"start": v(-8.72, 6.57) * mm, "end": v(-8.69, 6.63) * mm});
            skLineSegment(sketch, "E413", {"start": v(-8.69, 6.63) * mm, "end": v(-8.68, 6.64) * mm});
            skLineSegment(sketch, "E414", {"start": v(-8.68, 6.64) * mm, "end": v(-8.67, 6.7) * mm});
            skLineSegment(sketch, "E415", {"start": v(-8.67, 6.7) * mm, "end": v(-8.68, 6.74) * mm});
            skLineSegment(sketch, "E416", {"start": v(-8.68, 6.74) * mm, "end": v(-8.71, 6.77) * mm});
            skLineSegment(sketch, "E417", {"start": v(-8.71, 6.77) * mm, "end": v(-8.74, 6.78) * mm});
            skLineSegment(sketch, "E418", {"start": v(-8.74, 6.78) * mm, "end": v(-8.75, 6.78) * mm});
            skLineSegment(sketch, "E419", {"start": v(-8.75, 6.78) * mm, "end": v(-8.91, 6.78) * mm});
            skLineSegment(sketch, "E420", {"start": v(-8.91, 6.78) * mm, "end": v(-8.91, 7.33) * mm});
            skLineSegment(sketch, "E421", {"start": v(-8.91, 7.33) * mm, "end": v(-7.51, 7.33) * mm});
            skLineSegment(sketch, "E422", {"start": v(-7.51, 7.33) * mm, "end": v(-7.51, 6.84) * mm});
            skLineSegment(sketch, "E423", {"start": v(-7.51, 6.84) * mm, "end": v(-7.56, 6.83) * mm});
            skLineSegment(sketch, "E424", {"start": v(-7.56, 6.83) * mm, "end": v(-7.7, 6.78) * mm});
            skLineSegment(sketch, "E425", {"start": v(-7.7, 6.78) * mm, "end": v(-7.84, 6.7) * mm});
            skLineSegment(sketch, "E426", {"start": v(-7.84, 6.7) * mm, "end": v(-7.96, 6.62) * mm});
            skLineSegment(sketch, "E427", {"start": v(-7.96, 6.62) * mm, "end": v(-8.03, 6.55) * mm});
            skLineSegment(sketch, "E428", {"start": v(-8.03, 6.55) * mm, "end": v(-8.05, 6.53) * mm});
            skLineSegment(sketch, "E429", {"start": v(-8.05, 6.53) * mm, "end": v(-8.07, 6.5) * mm});
            skLineSegment(sketch, "E430", {"start": v(-8.07, 6.5) * mm, "end": v(-8.16, 6.38) * mm});
            skLineSegment(sketch, "E431", {"start": v(-8.16, 6.38) * mm, "end": v(-8.23, 6.24) * mm});
            skLineSegment(sketch, "E432", {"start": v(-8.23, 6.24) * mm, "end": v(-8.24, 6.22) * mm});
            skLineSegment(sketch, "E433", {"start": v(-8.24, 6.22) * mm, "end": v(-8.27, 6.16) * mm});
            skLineSegment(sketch, "E434", {"start": v(-8.27, 6.16) * mm, "end": v(-8.34, 5.97) * mm});
            skLineSegment(sketch, "E435", {"start": v(-8.34, 5.97) * mm, "end": v(-8.43, 5.66) * mm});
            skLineSegment(sketch, "E436", {"start": v(-8.43, 5.66) * mm, "end": v(-8.48, 5.3) * mm});
            skLineSegment(sketch, "E437", {"start": v(-8.48, 5.3) * mm, "end": v(-8.5, 5) * mm});
            skLineSegment(sketch, "E438", {"start": v(-8.5, 5) * mm, "end": v(-8.5, 4.9) * mm});
            skLineSegment(sketch, "E439", {"start": v(-8.5, 4.9) * mm, "end": v(-8.5, 4.82) * mm});
            skLineSegment(sketch, "E440", {"start": v(-8.5, 4.82) * mm, "end": v(-8.49, 4.57) * mm});
            skLineSegment(sketch, "E441", {"start": v(-8.49, 4.57) * mm, "end": v(-8.44, 4.25) * mm});
            skLineSegment(sketch, "E442", {"start": v(-8.44, 4.25) * mm, "end": v(-8.37, 3.98) * mm});
            skLineSegment(sketch, "E443", {"start": v(-8.37, 3.98) * mm, "end": v(-8.3, 3.83) * mm});
            skLineSegment(sketch, "E444", {"start": v(-8.3, 3.83) * mm, "end": v(-8.27, 3.78) * mm});
            skLineSegment(sketch, "E445", {"start": v(-8.27, 3.78) * mm, "end": v(-8.25, 3.75) * mm});
            skLineSegment(sketch, "E446", {"start": v(-8.25, 3.75) * mm, "end": v(-8.12, 3.62) * mm});
            skLineSegment(sketch, "E447", {"start": v(-8.12, 3.62) * mm, "end": v(-7.98, 3.57) * mm});
            skLineSegment(sketch, "E448", {"start": v(-7.98, 3.57) * mm, "end": v(-7.94, 3.57) * mm});
            skLineSegment(sketch, "E449", {"start": v(-7.94, 3.57) * mm, "end": v(-7.9, 3.57) * mm});
            skLineSegment(sketch, "E450", {"start": v(-7.9, 3.57) * mm, "end": v(-7.82, 3.6) * mm});
            skLineSegment(sketch, "E451", {"start": v(-7.82, 3.6) * mm, "end": v(-7.74, 3.66) * mm});
            skLineSegment(sketch, "E452", {"start": v(-7.74, 3.66) * mm, "end": v(-7.68, 3.73) * mm});
            skLineSegment(sketch, "E453", {"start": v(-7.68, 3.73) * mm, "end": v(-7.66, 3.78) * mm});
            skLineSegment(sketch, "E454", {"start": v(-7.66, 3.78) * mm, "end": v(-7.65, 3.8) * mm});
            skLineSegment(sketch, "E455", {"start": v(-7.65, 3.8) * mm, "end": v(-7.63, 3.86) * mm});
            skLineSegment(sketch, "E456", {"start": v(-7.63, 3.86) * mm, "end": v(-7.6, 4.05) * mm});
            skLineSegment(sketch, "E457", {"start": v(-7.6, 4.05) * mm, "end": v(-7.55, 4.37) * mm});
            skLineSegment(sketch, "E458", {"start": v(-7.55, 4.37) * mm, "end": v(-7.51, 4.72) * mm});
            skLineSegment(sketch, "E459", {"start": v(-7.51, 4.72) * mm, "end": v(-7.49, 4.95) * mm});
            skLineSegment(sketch, "E460", {"start": v(-7.49, 4.95) * mm, "end": v(-7.48, 5.03) * mm});
            skSolve(sketch);
        }
        {
            var Q0;
            Q0 = qSketchRegion(id + "F4", true);
            extrude(context, id + "F5", {"entities" : qUnion([Q0]), "operationType" : NewBodyOperationType.REMOVE, "oppositeDirection" : true, "depth" : .5 * mm});
        }
        {
            var Q0;
            Q0=makeQuery(id+"F3.opExtrude","CAP_EDGE",EDGE,{"disambiguationData":[OSD([sQuery(id+"F2.wireOp",EDGE,"E12.right")])],"isStart":true});
            var Q1;
            Q1=makeQuery(id+"F3.opExtrude","CAP_EDGE",EDGE,{"disambiguationData":[OSD([sQuery(id+"F2.wireOp",EDGE,"E12.left")])],"isStart":true});
            fillet(context, id + "F6", {"entities" : qUnion([Q0, Q1]), "radius" : 2 * mm, "tangentPropagation" : true, "allowEdgeOverflow" : false});
        }
        {
            var Q0;
            {var subQ0=sQuery(id+"F0.wireOp",EDGE,"E7");Q0=makeQuery(id+"F6.opFillet","TWEAK_EDGE",EDGE,{"derivedFrom":[makeQuery(id+"F3.boolean.opBoolean","MERGE",VERTEX,{"derivedFrom":[makeQuery(id+"F1.opExtrude","CAP_VERTEX",VERTEX,{"disambiguationData":[OSD([sQuery(id+"F0.wireOp",EDGE,"E1"),subQ0])],"isStart":false}),makeQuery(id+"F3.opExtrude","CAP_VERTEX",VERTEX,{"disambiguationData":[OSD([subQ0,sQuery(id+"F2.wireOp",EDGE,"E12.top"),sQuery(id+"F2.wireOp",EDGE,"E12.right")])],"isStart":true})]})]});}
            var Q1;
            {var subQ0=sQuery(id+"F0.wireOp",EDGE,"E11.trimOffspring");Q1=makeQuery(id+"F6.opFillet","TWEAK_EDGE",EDGE,{"derivedFrom":[makeQuery(id+"F3.boolean.opBoolean","MERGE",VERTEX,{"derivedFrom":[makeQuery(id+"F1.opExtrude","CAP_VERTEX",VERTEX,{"disambiguationData":[OSD([sQuery(id+"F0.wireOp",EDGE,"E1"),subQ0])],"isStart":false}),makeQuery(id+"F3.opExtrude","CAP_VERTEX",VERTEX,{"disambiguationData":[OSD([subQ0,sQuery(id+"F2.wireOp",EDGE,"E12.top"),sQuery(id+"F2.wireOp",EDGE,"E12.left")])],"isStart":true})]})]});}
            fillet(context, id + "F7", {"entities" : qUnion([Q0, Q1]), "radius" : 2 * mm, "tangentPropagation" : true, "allowEdgeOverflow" : false});
        }
        {
            var Q0;
            Q0=makeQuery(id+"F1.opExtrude","SWEPT_EDGE",EDGE,{"disambiguationData":[OSD([sQuery(id+"F0.wireOp",EDGE,"E0"),sQuery(id+"F0.wireOp",EDGE,"E6")])]});
            chamfer(context, id + "F8", {"entities" : qUnion([Q0]), "chamferType" : ChamferType.TWO_OFFSETS, "width1" : 1 * mm, "oppositeDirection" : false, "width2" : 2.5 * mm, "tangentPropagation" : true});
        }
        {
            var Q0;
            Q0=makeQuery(id+"F1.opExtrude","SWEPT_EDGE",EDGE,{"disambiguationData":[OSD([sQuery(id+"F0.wireOp",EDGE,"E3"),sQuery(id+"F0.wireOp",EDGE,"E4")])]});
            var Q1;
            Q1=makeQuery(id+"F1.opExtrude","SWEPT_EDGE",EDGE,{"disambiguationData":[OSD([sQuery(id+"F0.wireOp",EDGE,"E4"),sQuery(id+"F0.wireOp",EDGE,"E5")])]});
            var Q2;
            Q2=makeQuery(id+"F3.opExtrude","CAP_EDGE",EDGE,{"disambiguationData":[OSD([sQuery(id+"F2.wireOp",EDGE,"E12.bottom")])],"isStart":false});
            var Q3;
            Q3=makeQuery(id+"F3.opExtrude","SWEPT_EDGE",EDGE,{"disambiguationData":[OSD([sQuery(id+"F0.wireOp",EDGE,"E4"),sQuery(id+"F2.wireOp",EDGE,"E12.bottom"),sQuery(id+"F2.wireOp",EDGE,"E12.right")])]});
            var Q4;
            Q4=makeQuery(id+"F3.opExtrude","SWEPT_EDGE",EDGE,{"disambiguationData":[OSD([sQuery(id+"F0.wireOp",EDGE,"E4"),sQuery(id+"F2.wireOp",EDGE,"E12.bottom"),sQuery(id+"F2.wireOp",EDGE,"E12.left")])]});
            var Q5;
            {var subQ1=sQuery(id+"F2.wireOp",EDGE,"E12.left");var subQ2=sQuery(id+"F2.wireOp",EDGE,"E12.bottom");var subQ3=sQuery(id+"F0.wireOp",EDGE,"E3");var subQ11=sQuery(id+"F0.wireOp",EDGE,"E4");Q5=makeQuery(id+"F6.opFillet","BLEND_EDGE",EDGE,{"blendedFrom":[makeQuery(id+"F3.opExtrude","CAP_EDGE",EDGE,{"disambiguationData":[OSD([subQ1])],"isStart":true}),makeQuery(id+"F5.boolean.opBoolean","SPLIT",FACE,{"disambiguationData":[TD([makeQuery(id+"F1.opExtrude","SWEPT_FACE",FACE,{"disambiguationData":[OSD([subQ3])]})])],"derivedFrom":makeQuery(id+"F3.boolean.opBoolean","MERGE",FACE,{"derivedFrom":[makeQuery(id+"F1.opExtrude","SWEPT_FACE",FACE,{"disambiguationData":[OSD([subQ11])]}),makeQuery(id+"F3.opExtrude","SWEPT_FACE",FACE,{"disambiguationData":[OSD([subQ2])]})]})})],"blendedInto":[makeQuery(id+"F5.boolean.opBoolean","SPLIT",FACE,{"disambiguationData":[TD([makeQuery(id+"F1.opExtrude","SWEPT_FACE",FACE,{"disambiguationData":[OSD([subQ3])]})])],"derivedFrom":makeQuery(id+"F3.boolean.opBoolean","MERGE",FACE,{"derivedFrom":[makeQuery(id+"F1.opExtrude","SWEPT_FACE",FACE,{"disambiguationData":[OSD([subQ11])]}),makeQuery(id+"F3.opExtrude","SWEPT_FACE",FACE,{"disambiguationData":[OSD([subQ2])]})]})})]});}
            var Q6;
            {var subQ0=sQuery(id+"F2.wireOp",EDGE,"E12.right");var subQ2=sQuery(id+"F2.wireOp",EDGE,"E12.bottom");var subQ3=sQuery(id+"F0.wireOp",EDGE,"E3");var subQ11=sQuery(id+"F0.wireOp",EDGE,"E4");Q6=makeQuery(id+"F6.opFillet","BLEND_EDGE",EDGE,{"blendedFrom":[makeQuery(id+"F3.opExtrude","CAP_EDGE",EDGE,{"disambiguationData":[OSD([subQ0])],"isStart":true}),makeQuery(id+"F5.boolean.opBoolean","SPLIT",FACE,{"disambiguationData":[TD([makeQuery(id+"F1.opExtrude","SWEPT_FACE",FACE,{"disambiguationData":[OSD([subQ3])]})])],"derivedFrom":makeQuery(id+"F3.boolean.opBoolean","MERGE",FACE,{"derivedFrom":[makeQuery(id+"F1.opExtrude","SWEPT_FACE",FACE,{"disambiguationData":[OSD([subQ11])]}),makeQuery(id+"F3.opExtrude","SWEPT_FACE",FACE,{"disambiguationData":[OSD([subQ2])]})]})})],"blendedInto":[makeQuery(id+"F5.boolean.opBoolean","SPLIT",FACE,{"disambiguationData":[TD([makeQuery(id+"F1.opExtrude","SWEPT_FACE",FACE,{"disambiguationData":[OSD([subQ3])]})])],"derivedFrom":makeQuery(id+"F3.boolean.opBoolean","MERGE",FACE,{"derivedFrom":[makeQuery(id+"F1.opExtrude","SWEPT_FACE",FACE,{"disambiguationData":[OSD([subQ11])]}),makeQuery(id+"F3.opExtrude","SWEPT_FACE",FACE,{"disambiguationData":[OSD([subQ2])]})]})})]});}
            var Q7;
            {var subQ0=sQuery(id+"F0.wireOp",EDGE,"E3");var subQ1=sQuery(id+"F0.wireOp",EDGE,"E4");Q7=makeQuery(id+"F3.boolean.opBoolean","SPLIT",EDGE,{"disambiguationData":[TD([makeQuery(id+"F1.opExtrude","SWEPT_FACE",FACE,{"disambiguationData":[OSD([subQ0])]})])],"derivedFrom":makeQuery(id+"F1.opExtrude","CAP_EDGE",EDGE,{"disambiguationData":[OSD([subQ1])],"isStart":false})});}
            var Q8;
            {var subQ0=sQuery(id+"F0.wireOp",EDGE,"E5");var subQ1=sQuery(id+"F0.wireOp",EDGE,"E4");Q8=makeQuery(id+"F3.boolean.opBoolean","SPLIT",EDGE,{"disambiguationData":[TD([makeQuery(id+"F1.opExtrude","SWEPT_FACE",FACE,{"disambiguationData":[OSD([subQ0])]})])],"derivedFrom":makeQuery(id+"F1.opExtrude","CAP_EDGE",EDGE,{"disambiguationData":[OSD([subQ1])],"isStart":false})});}
            fillet(context, id + "F9", {"entities" : qUnion([Q0, Q1, Q2, Q3, Q4, Q5, Q6, Q7, Q8]), "radius" : 1 * mm, "tangentPropagation" : true, "allowEdgeOverflow" : false});
        }
    });
